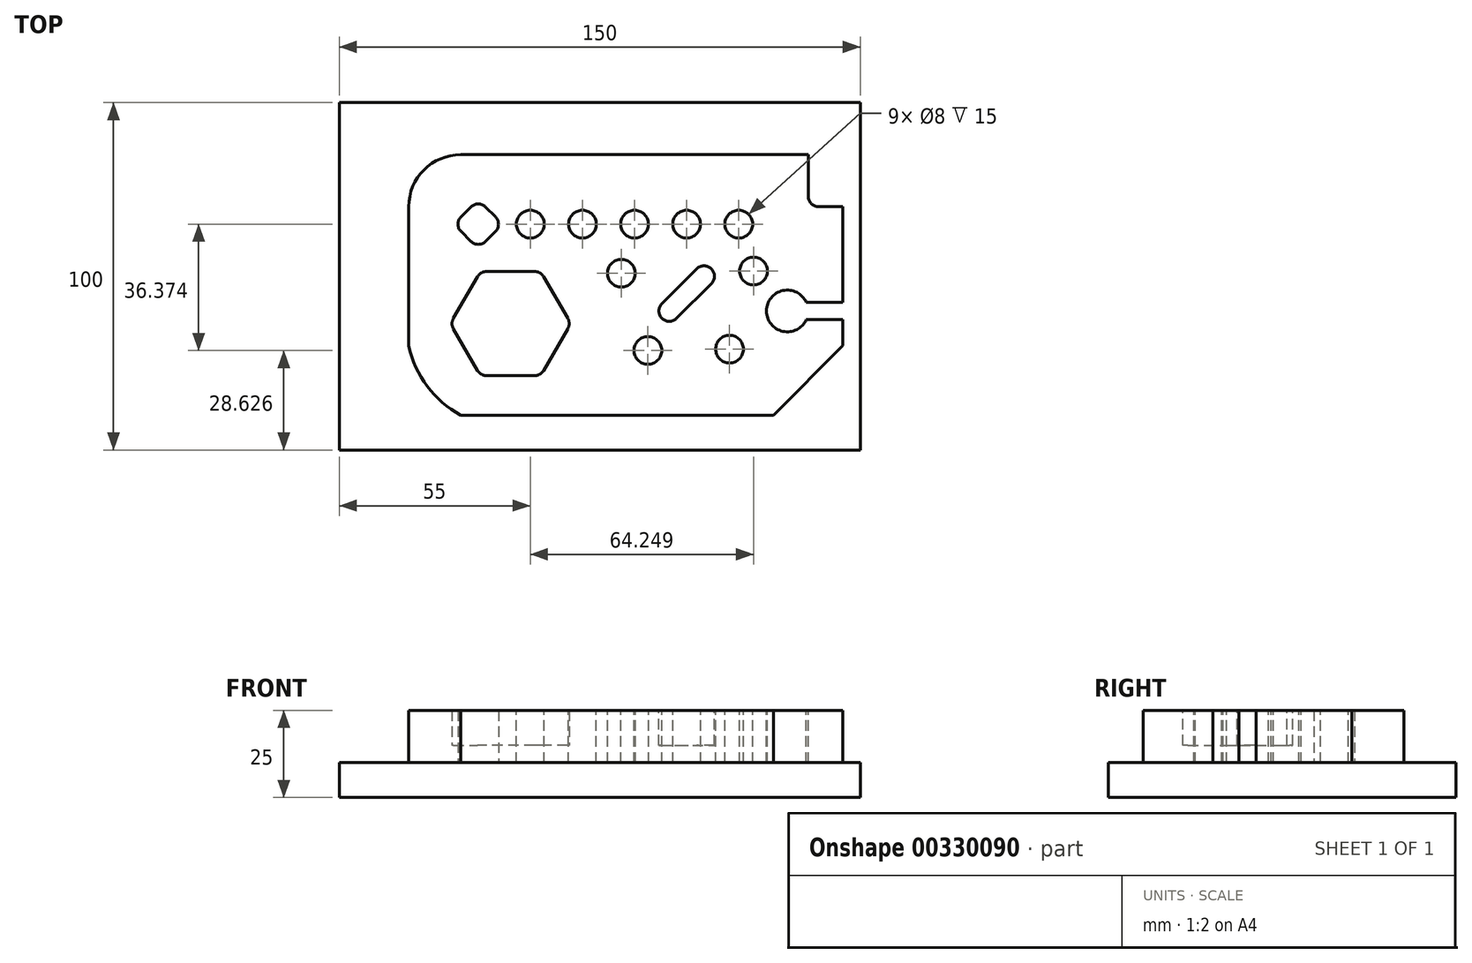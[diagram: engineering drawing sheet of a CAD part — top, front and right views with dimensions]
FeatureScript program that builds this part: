
annotation { "Feature Type Name" : "Feature", "Feature Type Description" : "" }
export const myFeature = defineFeature(function(context is Context, id is Id, definition is map)
    precondition{}
    {
        {
            var Q0;
            Q0=qCreatedBy(makeId("Top.planeOp"),FACE);
            cPlane(context, id + "F0", {"entities" : qUnion([Q0]), "cplaneType" : CPlaneType.OFFSET, "offset" : 0 * mm, "width" : 152.4 * mm, "height" : 152.4 * mm});
        }
        {
            var Q0;
            Q0=qCreatedBy(id+"F0.planeOp",FACE);
            var sketch = newSketch(context, id + "F1", { "sketchPlane" : qUnion([Q0])});
            skLineSegment(sketch, "E0.bottom", {"start": v(0, 0) * mm, "end": v(150, 0) * mm});
            skLineSegment(sketch, "E0.top", {"start": v(0, 100) * mm, "end": v(150, 100) * mm});
            skLineSegment(sketch, "E0.left", {"start": v(0, 0) * mm, "end": v(0, 100) * mm});
            skLineSegment(sketch, "E0.right", {"start": v(150, 0) * mm, "end": v(150, 100) * mm});
            skSolve(sketch);
        }
        {
            var Q0;
            Q0 = qSketchRegion(id + "F1", true);
            extrude(context, id + "F2", {"entities" : qUnion([Q0]), "depth" : 10 * mm});
        }
        {
            var Q0;
            Q0=makeQuery(id+"F2.opExtrude","CAP_FACE",FACE,{"disambiguationData":[OSD([sQuery(id+"F1.wireOp",EDGE,"E0.bottom"),sQuery(id+"F1.wireOp",EDGE,"E0.top"),sQuery(id+"F1.wireOp",EDGE,"E0.left"),sQuery(id+"F1.wireOp",EDGE,"E0.right")])],"isStart":false});
            var sketch = newSketch(context, id + "F3", { "sketchPlane" : qUnion([Q0])});
            skLineSegment(sketch, "E1.bottom", {"start": v(20, 10) * mm, "end": v(145, 10) * mm});
            skLineSegment(sketch, "E1.top", {"start": v(20, 85) * mm, "end": v(145, 85) * mm});
            skLineSegment(sketch, "E1.left", {"start": v(20, 10) * mm, "end": v(20, 85) * mm});
            skLineSegment(sketch, "E1.right", {"start": v(145, 10) * mm, "end": v(145, 85) * mm});
            skSolve(sketch);
        }
        {
            var Q0;
            Q0 = qSketchRegion(id + "F3", true);
            extrude(context, id + "F4", {"entities" : qUnion([Q0]), "operationType" : NewBodyOperationType.ADD, "depth" : 15 * mm});
        }
        {
            var Q0;
            Q0=makeQuery(id+"F4.opExtrude","SWEPT_EDGE",EDGE,{"disambiguationData":[OSD([sQuery(id+"F3.wireOp",EDGE,"E1.top"),sQuery(id+"F3.wireOp",EDGE,"E1.left")])]});
            fillet(context, id + "F5", {"entities" : qUnion([Q0]), "radius" : 15 * mm, "tangentPropagation" : true, "allowEdgeOverflow" : false});
        }
        {
            var Q0;
            Q0=makeQuery(id+"F4.opExtrude","SWEPT_EDGE",EDGE,{"disambiguationData":[OSD([sQuery(id+"F3.wireOp",EDGE,"E1.bottom"),sQuery(id+"F3.wireOp",EDGE,"E1.right")])]});
            chamfer(context, id + "F6", {"entities" : qUnion([Q0]), "width" : 20 * mm, "tangentPropagation" : true});
        }
        {
            var Q0;
            Q0=makeQuery(id+"F4.opExtrude","CAP_FACE",FACE,{"disambiguationData":[OSD([sQuery(id+"F3.wireOp",EDGE,"E1.bottom"),sQuery(id+"F3.wireOp",EDGE,"E1.top"),sQuery(id+"F3.wireOp",EDGE,"E1.left"),sQuery(id+"F3.wireOp",EDGE,"E1.right")])],"isStart":false});
            var sketch = newSketch(context, id + "F7", { "sketchPlane" : qUnion([Q0])});
            skLineSegment(sketch, "E2.bottom", {"start": v(145, 85) * mm, "end": v(135, 85) * mm});
            skLineSegment(sketch, "E2.top", {"start": v(145, 70) * mm, "end": v(135, 70) * mm});
            skLineSegment(sketch, "E2.left", {"start": v(145, 85) * mm, "end": v(145, 70) * mm});
            skLineSegment(sketch, "E2.right", {"start": v(135, 85) * mm, "end": v(135, 70) * mm});
            skSolve(sketch);
        }
        {
            var Q0;
            Q0 = qSketchRegion(id + "F7", true);
            extrude(context, id + "F8", {"entities" : qUnion([Q0]), "operationType" : NewBodyOperationType.REMOVE, "oppositeDirection" : true, "depth" : 15 * mm});
        }
        {
            var Q0;
            Q0=makeQuery(id+"F4.opExtrude","CAP_FACE",FACE,{"disambiguationData":[OSD([sQuery(id+"F3.wireOp",EDGE,"E1.bottom"),sQuery(id+"F3.wireOp",EDGE,"E1.top"),sQuery(id+"F3.wireOp",EDGE,"E1.left"),sQuery(id+"F3.wireOp",EDGE,"E1.right")])],"isStart":false});
            var sketch = newSketch(context, id + "F9", { "sketchPlane" : qUnion([Q0])});
            skCircle(sketch, "E3", {"center": v(49.32, 36.36) * mm, "radius": 30 * mm});
            skPoint(sketch, "E3.first.point", {"position": v(20, 30) * mm});
            skPoint(sketch, "E3.second.point", {"position": v(35, 10) * mm});
            skPoint(sketch, "E3.third.point", {"position": v(29.9, 13.5) * mm});
            skLineSegment(sketch, "E4", {"start": v(20, 30) * mm, "end": v(20, 10) * mm});
            skLineSegment(sketch, "E5", {"start": v(20, 10) * mm, "end": v(35, 10) * mm});
            skSolve(sketch);
        }
        {
            var Q0;
            {var subQ0=sQuery(id+"F9.wireOp",EDGE,"E4");Q0=makeQuery(id+"F9.imprint","IMPRINT",FACE,{"disambiguationData":[TD([[makeQuery(id+"F9.imprint","IMPRINT",EDGE,{"derivedFrom":subQ0}),-1.0]])]});}
            var Q1;
            Q1=makeQuery(id+"F8.boolean.opBoolean","MERGE",FACE,{"derivedFrom":[makeQuery(id+"F2.opExtrude","CAP_FACE",FACE,{"disambiguationData":[OSD([sQuery(id+"F1.wireOp",EDGE,"E0.bottom"),sQuery(id+"F1.wireOp",EDGE,"E0.top"),sQuery(id+"F1.wireOp",EDGE,"E0.left"),sQuery(id+"F1.wireOp",EDGE,"E0.right")])],"isStart":false}),makeQuery(id+"F8.opExtrude","CAP_FACE",FACE,{"disambiguationData":[OSD([sQuery(id+"F7.wireOp",EDGE,"E2.bottom"),sQuery(id+"F7.wireOp",EDGE,"E2.top"),sQuery(id+"F7.wireOp",EDGE,"E2.left"),sQuery(id+"F7.wireOp",EDGE,"E2.right")])],"isStart":false})]});
            extrude(context, id + "F10", {"entities" : qUnion([Q0]), "operationType" : NewBodyOperationType.REMOVE, "endBound" : BoundingType.UP_TO_SURFACE, "oppositeDirection" : true, "endBoundEntityFace" : qUnion([Q1]), "depth" : 25.4 * mm});
        }
        {
            var Q0;
            Q0=makeQuery(id+"F4.opExtrude","CAP_FACE",FACE,{"disambiguationData":[OSD([sQuery(id+"F3.wireOp",EDGE,"E1.bottom"),sQuery(id+"F3.wireOp",EDGE,"E1.top"),sQuery(id+"F3.wireOp",EDGE,"E1.left"),sQuery(id+"F3.wireOp",EDGE,"E1.right")])],"isStart":false});
            var sketch = newSketch(context, id + "F11", { "sketchPlane" : qUnion([Q0])});
            skCircle(sketch, "E6", {"center": v(55, 65) * mm, "radius": 4 * mm});
            skCircle(sketch, "E7", {"center": v(70, 65) * mm, "radius": 4 * mm});
            skCircle(sketch, "E8", {"center": v(85, 65) * mm, "radius": 4 * mm});
            skCircle(sketch, "E9", {"center": v(100, 65) * mm, "radius": 4 * mm});
            skCircle(sketch, "E10", {"center": v(115, 65) * mm, "radius": 4 * mm});
            skCircle(sketch, "E11.1.0", {"center": v(119.25, 51.5) * mm, "radius": 4 * mm});
            skCircle(sketch, "E11.2.0", {"center": v(112.35, 29.01) * mm, "radius": 4 * mm});
            skPoint(sketch, "E11.center", {"position": v(100.33, 45) * mm});
            skLineSegment(sketch, "E11.anchor1", {"start": v(100.33, 45) * mm, "end": v(100, 65) * mm, "construction": true});
            skLineSegment(sketch, "E11.anchor2", {"start": v(100.33, 45) * mm, "end": v(112.35, 29.01) * mm, "construction": true});
            skCircle(sketch, "E12.1.0", {"center": v(88.84, 28.63) * mm, "radius": 4 * mm});
            skCircle(sketch, "E12.2.0", {"center": v(81.2, 50.87) * mm, "radius": 4 * mm});
            skLineSegment(sketch, "E12.anchor2", {"start": v(100.33, 45) * mm, "end": v(81.2, 50.87) * mm, "construction": true});
            skSolve(sketch);
        }
        {
            var Q0;
            Q0 = qSketchRegion(id + "F11", true);
            extrude(context, id + "F12", {"entities" : qUnion([Q0]), "operationType" : NewBodyOperationType.REMOVE, "oppositeDirection" : true, "depth" : 15 * mm});
        }
        {
            var Q0;
            Q0=makeQuery(id+"F4.opExtrude","CAP_FACE",FACE,{"disambiguationData":[OSD([sQuery(id+"F3.wireOp",EDGE,"E1.bottom"),sQuery(id+"F3.wireOp",EDGE,"E1.top"),sQuery(id+"F3.wireOp",EDGE,"E1.left"),sQuery(id+"F3.wireOp",EDGE,"E1.right")])],"isStart":false});
            var sketch = newSketch(context, id + "F13", { "sketchPlane" : qUnion([Q0])});
            skLineSegment(sketch, "E13", {"start": v(32.93, 65) * mm, "end": v(40, 72.07) * mm});
            skLineSegment(sketch, "E14", {"start": v(40, 72.07) * mm, "end": v(47.07, 65) * mm});
            skLineSegment(sketch, "E15", {"start": v(47.07, 65) * mm, "end": v(40, 57.93) * mm});
            skLineSegment(sketch, "E16", {"start": v(40, 57.93) * mm, "end": v(32.93, 65) * mm});
            skSolve(sketch);
        }
        {
            var Q0;
            Q0 = qSketchRegion(id + "F13", true);
            extrude(context, id + "F14", {"entities" : qUnion([Q0]), "operationType" : NewBodyOperationType.REMOVE, "oppositeDirection" : true, "depth" : 15 * mm});
        }
        {
            var Q0;
            Q0=makeQuery(id+"F4.opExtrude","CAP_FACE",FACE,{"disambiguationData":[OSD([sQuery(id+"F3.wireOp",EDGE,"E1.bottom"),sQuery(id+"F3.wireOp",EDGE,"E1.top"),sQuery(id+"F3.wireOp",EDGE,"E1.left"),sQuery(id+"F3.wireOp",EDGE,"E1.right")])],"isStart":false});
            var sketch = newSketch(context, id + "F15", { "sketchPlane" : qUnion([Q0])});
            skLineSegment(sketch, "E17.bottom", {"start": v(145, 37.5) * mm, "end": v(129, 37.5) * mm});
            skLineSegment(sketch, "E17.top", {"start": v(145, 42.5) * mm, "end": v(129, 42.5) * mm});
            skLineSegment(sketch, "E17.left", {"start": v(145, 37.5) * mm, "end": v(145, 42.5) * mm});
            skLineSegment(sketch, "E17.right", {"start": v(129, 37.5) * mm, "end": v(129, 42.5) * mm});
            skCircle(sketch, "E18", {"center": v(129, 40) * mm, "radius": 6 * mm});
            skSolve(sketch);
        }
        {
            var Q0;
            Q0 = qSketchRegion(id + "F15", true);
            extrude(context, id + "F16", {"entities" : qUnion([Q0]), "operationType" : NewBodyOperationType.REMOVE, "oppositeDirection" : true, "depth" : 15 * mm});
        }
        {
            var Q0;
            Q0=makeQuery(id+"F4.opExtrude","CAP_FACE",FACE,{"disambiguationData":[OSD([sQuery(id+"F3.wireOp",EDGE,"E1.bottom"),sQuery(id+"F3.wireOp",EDGE,"E1.top"),sQuery(id+"F3.wireOp",EDGE,"E1.left"),sQuery(id+"F3.wireOp",EDGE,"E1.right")])],"isStart":false});
            var sketch = newSketch(context, id + "F17", { "sketchPlane" : qUnion([Q0])});
            skLineSegment(sketch, "E19", {"start": v(92.88, 42.12) * mm, "end": v(102.88, 52.12) * mm});
            skLineSegment(sketch, "E20", {"start": v(97.12, 37.88) * mm, "end": v(107.12, 47.88) * mm});
            skCircle(sketch, "E21", {"center": v(105, 50) * mm, "radius": 3 * mm});
            skCircle(sketch, "E22", {"center": v(95, 40) * mm, "radius": 3 * mm});
            skSolve(sketch);
        }
        {
            var Q0;
            Q0 = qSketchRegion(id + "F17", true);
            extrude(context, id + "F18", {"entities" : qUnion([Q0]), "operationType" : NewBodyOperationType.REMOVE, "oppositeDirection" : true, "depth" : 10 * mm});
        }
        {
            var Q0;
            Q0=makeQuery(id+"F4.opExtrude","CAP_FACE",FACE,{"disambiguationData":[OSD([sQuery(id+"F3.wireOp",EDGE,"E1.bottom"),sQuery(id+"F3.wireOp",EDGE,"E1.top"),sQuery(id+"F3.wireOp",EDGE,"E1.left"),sQuery(id+"F3.wireOp",EDGE,"E1.right")])],"isStart":false});
            var sketch = newSketch(context, id + "F19", { "sketchPlane" : qUnion([Q0])});
            skCircle(sketch, "E23.cCircle", {"center": v(49.32, 36.36) * mm, "radius": 15 * mm, "construction": true});
            skLineSegment(sketch, "E23.0", {"start": v(32, 36.36) * mm, "end": v(40.66, 51.36) * mm});
            skLineSegment(sketch, "E23.1", {"start": v(40.66, 51.36) * mm, "end": v(57.98, 51.36) * mm});
            skLineSegment(sketch, "E23.2", {"start": v(57.98, 51.36) * mm, "end": v(66.64, 36.36) * mm});
            skLineSegment(sketch, "E23.3", {"start": v(66.64, 36.36) * mm, "end": v(57.98, 21.36) * mm});
            skLineSegment(sketch, "E23.4", {"start": v(57.98, 21.36) * mm, "end": v(40.66, 21.36) * mm});
            skLineSegment(sketch, "E23.5", {"start": v(40.66, 21.36) * mm, "end": v(32, 36.36) * mm});
            skPoint(sketch, "E23.0.midPoint", {"position": v(36.33, 43.86) * mm});
            skSolve(sketch);
        }
        {
            var Q0;
            Q0 = qSketchRegion(id + "F19", true);
            extrude(context, id + "F20", {"entities" : qUnion([Q0]), "operationType" : NewBodyOperationType.REMOVE, "oppositeDirection" : true, "depth" : 10 * mm});
        }
        {
            var Q0;
            Q0=makeQuery(id+"F14.boolean.opBoolean","COPY",EDGE,{"derivedFrom":makeQuery(id+"F14.opExtrude","SWEPT_EDGE",EDGE,{"disambiguationData":[OSD([sQuery(id+"F13.wireOp",EDGE,"E13"),sQuery(id+"F13.wireOp",EDGE,"E16")])]})});
            var Q1;
            Q1=makeQuery(id+"F14.boolean.opBoolean","COPY",EDGE,{"derivedFrom":makeQuery(id+"F14.opExtrude","SWEPT_EDGE",EDGE,{"disambiguationData":[OSD([sQuery(id+"F13.wireOp",EDGE,"E13"),sQuery(id+"F13.wireOp",EDGE,"E14")])]})});
            var Q2;
            Q2=makeQuery(id+"F14.boolean.opBoolean","COPY",EDGE,{"derivedFrom":makeQuery(id+"F14.opExtrude","SWEPT_EDGE",EDGE,{"disambiguationData":[OSD([sQuery(id+"F13.wireOp",EDGE,"E14"),sQuery(id+"F13.wireOp",EDGE,"E15")])]})});
            var Q3;
            Q3=makeQuery(id+"F14.boolean.opBoolean","COPY",EDGE,{"derivedFrom":makeQuery(id+"F14.opExtrude","SWEPT_EDGE",EDGE,{"disambiguationData":[OSD([sQuery(id+"F13.wireOp",EDGE,"E15"),sQuery(id+"F13.wireOp",EDGE,"E16")])]})});
            var Q4;
            Q4=makeQuery(id+"F20.boolean.opBoolean","COPY",EDGE,{"derivedFrom":makeQuery(id+"F20.opExtrude","SWEPT_EDGE",EDGE,{"disambiguationData":[OSD([sQuery(id+"F19.wireOp",EDGE,"E23.1"),sQuery(id+"F19.wireOp",EDGE,"E23.2")])]})});
            var Q5;
            Q5=makeQuery(id+"F20.boolean.opBoolean","COPY",EDGE,{"derivedFrom":makeQuery(id+"F20.opExtrude","SWEPT_EDGE",EDGE,{"disambiguationData":[OSD([sQuery(id+"F19.wireOp",EDGE,"E23.0"),sQuery(id+"F19.wireOp",EDGE,"E23.1")])]})});
            var Q6;
            Q6=makeQuery(id+"F20.boolean.opBoolean","COPY",EDGE,{"derivedFrom":makeQuery(id+"F20.opExtrude","SWEPT_EDGE",EDGE,{"disambiguationData":[OSD([sQuery(id+"F19.wireOp",EDGE,"E23.0"),sQuery(id+"F19.wireOp",EDGE,"E23.5")])]})});
            var Q7;
            Q7=makeQuery(id+"F20.boolean.opBoolean","COPY",EDGE,{"derivedFrom":makeQuery(id+"F20.opExtrude","SWEPT_EDGE",EDGE,{"disambiguationData":[OSD([sQuery(id+"F19.wireOp",EDGE,"E23.4"),sQuery(id+"F19.wireOp",EDGE,"E23.5")])]})});
            var Q8;
            Q8=makeQuery(id+"F20.boolean.opBoolean","COPY",EDGE,{"derivedFrom":makeQuery(id+"F20.opExtrude","SWEPT_EDGE",EDGE,{"disambiguationData":[OSD([sQuery(id+"F19.wireOp",EDGE,"E23.3"),sQuery(id+"F19.wireOp",EDGE,"E23.4")])]})});
            var Q9;
            Q9=makeQuery(id+"F20.boolean.opBoolean","COPY",EDGE,{"derivedFrom":makeQuery(id+"F20.opExtrude","SWEPT_EDGE",EDGE,{"disambiguationData":[OSD([sQuery(id+"F19.wireOp",EDGE,"E23.2"),sQuery(id+"F19.wireOp",EDGE,"E23.3")])]})});
            fillet(context, id + "F21", {"entities" : qUnion([Q0, Q1, Q2, Q3, Q4, Q5, Q6, Q7, Q8, Q9]), "radius" : 3 * mm, "tangentPropagation" : true, "allowEdgeOverflow" : false});
        }
        {
            var Q0;
            Q0=makeQuery(id+"F8.boolean.opBoolean","COPY",EDGE,{"derivedFrom":makeQuery(id+"F8.opExtrude","SWEPT_EDGE",EDGE,{"disambiguationData":[OSD([sQuery(id+"F7.wireOp",EDGE,"E2.top"),sQuery(id+"F7.wireOp",EDGE,"E2.right")])]})});
            fillet(context, id + "F22", {"entities" : qUnion([Q0]), "radius" : 3 * mm, "tangentPropagation" : true, "allowEdgeOverflow" : false});
        }
    });
